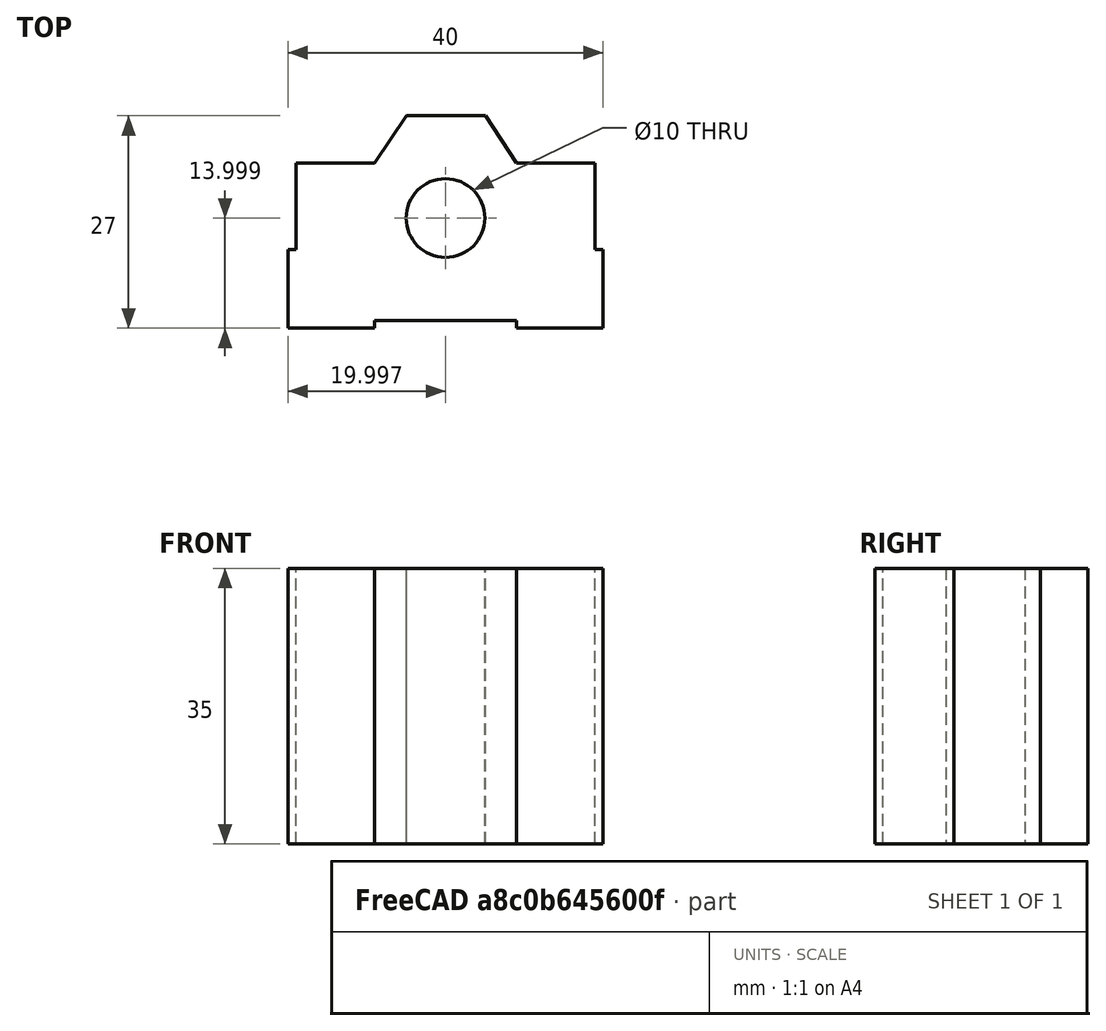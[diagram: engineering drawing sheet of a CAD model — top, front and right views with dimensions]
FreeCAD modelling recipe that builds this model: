
FCSTD DOCUMENT  (FreeCAD 0.17R13522 (Git))
Label: SC10UUBlocoRolamento
License: All rights reserved
LicenseURL: http://en.wikipedia.org/wiki/All_rights_reserved
objects: Sketcher::SketchObject×1, Part::Extrusion×1
note: 2 computed .brp shape members not serialized (recipe doc carries the construction recipe); baked Part::Feature solids carry a one-line shape summary decoded from their .brp

FEATURE [Sketcher::SketchObject] Sketch
  sketch-geometry (17):
    g0: LineSegment StartX=35.5374 StartY=23.1087 StartZ=0 EndX=35.5374 EndY=33.1087 EndZ=0
    g1: LineSegment StartX=35.5374 StartY=33.1087 StartZ=0 EndX=36.5374 EndY=33.1087 EndZ=0
    g2: LineSegment StartX=36.5374 StartY=33.1087 StartZ=0 EndX=36.5374 EndY=44.1087 EndZ=0
    g3: LineSegment StartX=36.5374 StartY=44.1087 StartZ=0 EndX=46.5374 EndY=44.1087 EndZ=0
    g4: LineSegment StartX=46.5374 StartY=44.1087 StartZ=0 EndX=50.6224 EndY=50.1087 EndZ=0
    g5: LineSegment StartX=50.6224 StartY=50.1087 StartZ=0 EndX=60.6224 EndY=50.1087 EndZ=0
    g6: LineSegment StartX=60.6224 StartY=50.1087 StartZ=0 EndX=64.5374 EndY=44.1087 EndZ=0
    g7: LineSegment StartX=64.5374 StartY=44.1087 StartZ=0 EndX=74.5374 EndY=44.1087 EndZ=0
    g8: LineSegment StartX=74.5374 StartY=44.1087 StartZ=0 EndX=74.5374 EndY=33.1087 EndZ=0
    g9: LineSegment StartX=74.5374 StartY=33.1087 StartZ=0 EndX=75.5374 EndY=33.1087 EndZ=0
    g10: LineSegment StartX=75.5374 StartY=33.1087 StartZ=0 EndX=75.5374 EndY=23.1087 EndZ=0
    g11: LineSegment StartX=75.5374 StartY=23.1087 StartZ=0 EndX=64.5374 EndY=23.1087 EndZ=0
    g12: LineSegment StartX=64.5374 StartY=23.1087 StartZ=0 EndX=64.5374 EndY=24.1087 EndZ=0
    g13: LineSegment StartX=64.5374 StartY=24.1087 StartZ=0 EndX=46.5374 EndY=24.1087 EndZ=0
    g14: LineSegment StartX=46.5374 StartY=24.1087 StartZ=0 EndX=46.5374 EndY=23.1087 EndZ=0
    g15: LineSegment StartX=46.5374 StartY=23.1087 StartZ=0 EndX=35.5374 EndY=23.1087 EndZ=0
    g16: Circle CenterX=55.5374 CenterY=37.1087 CenterZ=0 NormalX=0 NormalY=0 NormalZ=1 AngleXU=0 Radius=5
  constraints (48):
    c: Coincident(g0,g1)
    c: Coincident(g1,g2)
    c: Vertical(g2)
    c: Coincident(g2,g3)
    c: Horizontal(g3)
    c: Coincident(g3,g4)
    c: Coincident(g4,g5)
    c: Horizontal(g5)
    c: Coincident(g5,g6)
    c: Coincident(g6,g7)
    c: Horizontal(g7)
    c: Coincident(g7,g8)
    c: Vertical(g8)
    c: Coincident(g8,g9)
    c: Coincident(g9,g10)
    c: Vertical(g10)
    c: Coincident(g10,g11)
    c: Horizontal(g11)
    c: Coincident(g11,g12)
    c: Coincident(g12,g13)
    c: Horizontal(g13)
    c: Coincident(g13,g14)
    c: Vertical(g14)
    c: Coincident(g14,g15)
    c: Coincident(g15,g0)
    c: Horizontal(g15)
    c: Horizontal(g1)
    c: Horizontal(g9)
    c: Vertical(g0)
    c: Vertical(g12)
    c: DistanceX(g11,g11) = 11
    c: Equal(g11,g15)
    c: DistanceY(g10,g10) = 10
    c: Equal(g0,g10)
    c: DistanceY(g8,g8) = 11
    c: Equal(g8,g2)
    c: DistanceX(g13,g13) = 18
    c: DistanceY(g12,g12) = 1
    c: Equal(g12,g14)
    c: DistanceX(g1,g1) = 1
    c: Equal(g1,g9)
    c: DistanceX(g5,g5) = 10
    c: DistanceX(g3,g3) = 10
    c: Equal(g3,g7)
    c: DistanceY(g6,g6) = 6
    c: Radius(g16) = 5
    c: Distance(g16,g5) = 13
    c: Distance(g16,g2) = 19
FEATURE [Part::Extrusion] Extrude  label="SC10UU"
  Base = -> Sketch
  Dir = (0,0,1)
  DirMode = 2
  FaceMakerClass = Part::FaceMakerBullseye
  LengthFwd = 35
  LengthRev = 0
  Solid = true
  Symmetric = false
